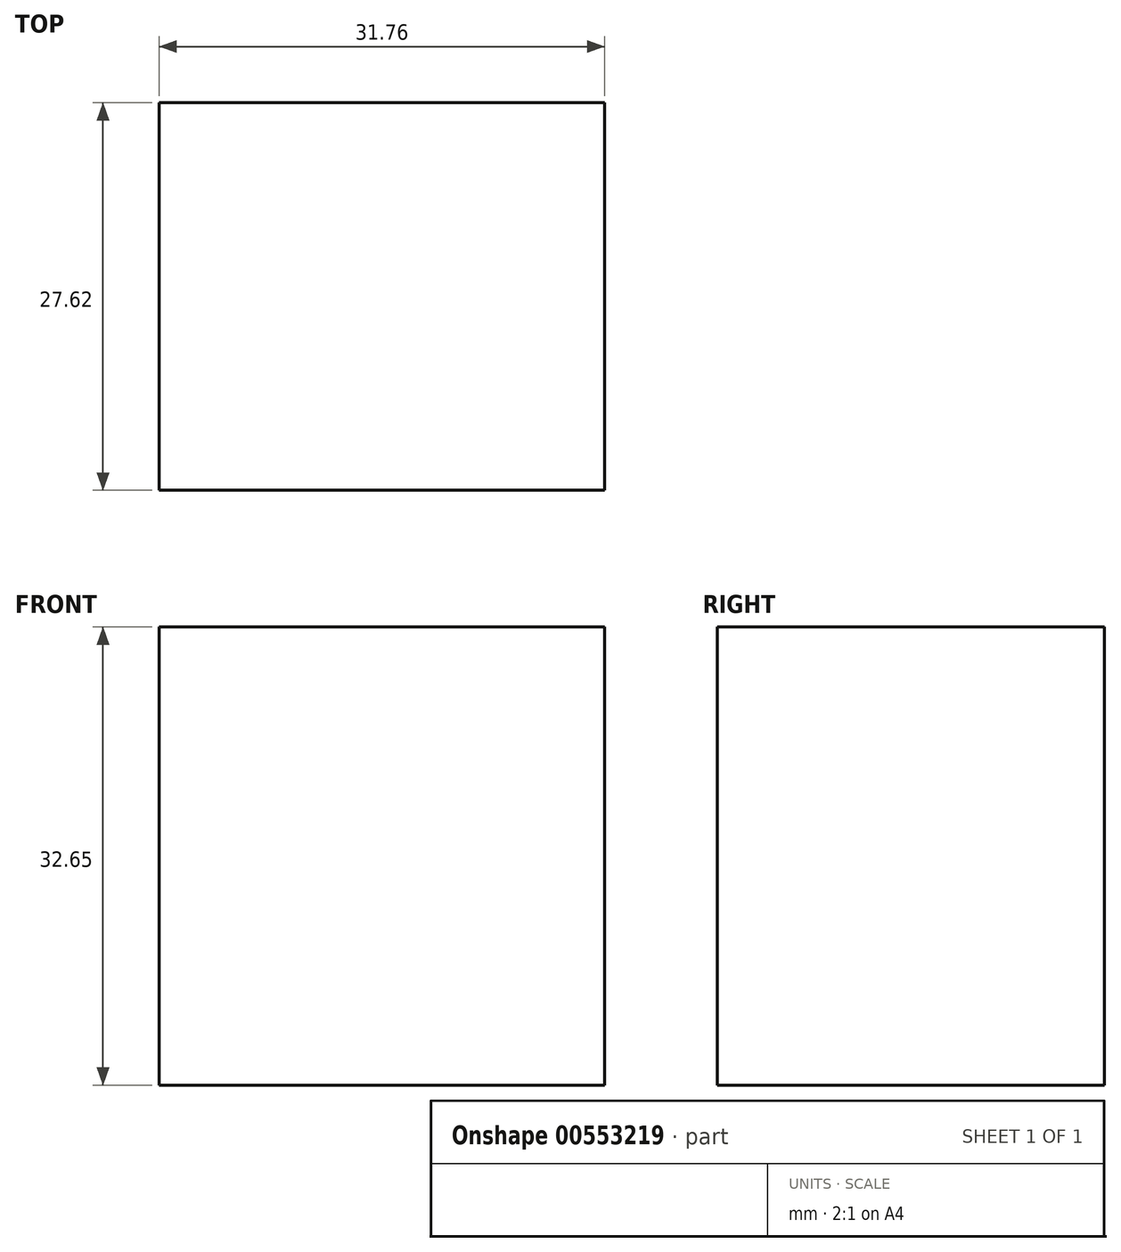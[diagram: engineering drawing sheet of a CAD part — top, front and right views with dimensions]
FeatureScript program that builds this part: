
annotation { "Feature Type Name" : "Feature", "Feature Type Description" : "" }
export const myFeature = defineFeature(function(context is Context, id is Id, definition is map)
    precondition{}
    {
        {
            var Q0;
            Q0=qCreatedBy(makeId("Top.planeOp"),FACE);
            var sketch = newSketch(context, id + "F0", { "sketchPlane" : qUnion([Q0])});
            skLineSegment(sketch, "E0.bottom", {"start": v(15.88, 13.8) * mm, "end": v(-15.88, 13.8) * mm});
            skLineSegment(sketch, "E0.top", {"start": v(15.88, -13.8) * mm, "end": v(-15.88, -13.8) * mm});
            skLineSegment(sketch, "E0.left", {"start": v(15.88, 13.8) * mm, "end": v(15.88, -13.8) * mm});
            skLineSegment(sketch, "E0.right", {"start": v(-15.88, 13.8) * mm, "end": v(-15.88, -13.8) * mm});
            skPoint(sketch, "E0.middle", {"position": v(0, 0) * mm});
            skSolve(sketch);
        }
        {
            var Q0;
            Q0=qCreatedBy(makeId("Front.planeOp"),FACE);
            var sketch = newSketch(context, id + "F1", { "sketchPlane" : qUnion([Q0])});
            skLineSegment(sketch, "E1", {"start": v(0, 0) * mm, "end": v(0, 32.65) * mm});
            skSolve(sketch);
        }
        {
            var Q0;
            Q0=makeQuery(id+"F0.imprint","IMPRINT",FACE,{"disambiguationData":[TD([[makeQuery(id+"F0.imprint","IMPRINT",EDGE,{"derivedFrom":sQuery(id+"F0.wireOp",EDGE,"E0.bottom")}),1.0]])]});
            var Q1;
            Q1=sQuery(id+"F1.wireOp",EDGE,"E1");
            sweep(context, id + "F2", {"profiles" : qUnion([Q0]), "path" : qUnion([Q1])});
        }
    });
